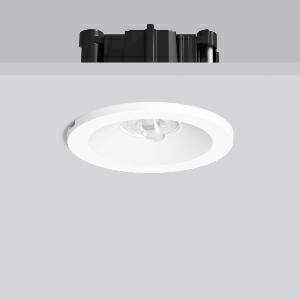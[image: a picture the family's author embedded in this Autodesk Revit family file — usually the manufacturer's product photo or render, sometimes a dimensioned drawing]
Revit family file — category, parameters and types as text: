
# Revit family: turia_l_672562_002_89_3b66
name_source: partatom
category: Lighting Fixtures
units: mm (PartAtom-declared; Revit-internal decimal feet)

## family parameters
Cut with Voids When Loaded = No
Host = Face
Light Source = No
Part Type = Normal
Room Calculation Point = No
Round Connector Dimension = Use Diameter
Shared = No

## types (1)
- TURIA L (1 x LED Modul 765, 250 lm, 6500)
    Apparent Load = 5 VA
    CIE Flux Codes = 70 91 99 100 100
    Color Rendering = 70
    Color Temperature = 6500
    Default Elevation = 1800 mm
    Description = Series: TURIA L
Round emergency luminaire for escape route lighting. With asymmetrical beam plastic lenses for illuminating rescue facilities. Suitable for connection to central battery systems. With MOM monitoring module for LPS (Low Power Supply) small central battery units of the type Easy+IP. With enclosed separate ceiling mounting ring also suitable for ceiling cut-outs of Ø 68 mm. 
Colour: white
Diameter: 62 mm
Height: 3 mm
Cut-out diameter: 54-68 mm
Recess height: 76-162 mm
Luminaire: recess height: 42 mm
Weight: 350 g
Operating mode: non-maintained power mode
Lamp: LED
Socket: without socket
Colour temperature: 6500K
Colour rendering index (CRI): 70
System power: 4.8 W
Rated luminous flux: 250 lm
Luminous flux, emergency: 250 lm
System power, emergency: 4.8 W
Control gear: Regulated power supply
Protection class: II
Type of protection: IP 20
    Height = 0 mm  [stored 0 ft]
    Lamp = 1 x LED Modul 765
    Lamp Light Flux = 250 lm
    Lamp count = 1
    Length = 62 mm  [stored 0.203412 ft]
    Lifetime = 50000 h
    Luminous efficacy = 52 lm/W
    Manufacturer = RZB
    ModVariant = No
    Model = 672562.002.89
    Mounting Place = Ceiling
    Mounting Type = Recessed
    Number of Poles = 1
    OnlyDefault = Yes
    Power Factor = 1
    Product Name = TURIA L
    Product group = Recessed ceiling luminaires
    ProductGroupID = 405
    Protection Class = Protection class II
    Protection Degree = IP 20
    RLX_Detail_Level = 1
    RLX_Emergency_Light_Flux = 250 lm
    RLX_Emergency_Type = 3
    RLX_Emergency_Type_DB = Yes
    RlxData = <blob elided: 54905 chars, md5=a9eec828>
    Socket = socket
    Standby Power = 0 W
    System Light Flux = 250 lm
    System Power = 5 W
    Type Comments = Product without accessories
    Type Image = 672561.002.jpg
    URL = http://relux.com
    VarID = ---
    Voltage = 230 V
    Voltage Range = 220-240 V
    Weight = 0.00 kg
    Width = 0 mm  [stored 0 ft]

note: [stored X ft] marks values corroborated as IEEE doubles in the binary element streams (Revit-internal decimal feet)

## geometry (parser evidence)
native form markers: Blend x4, Sweep x10
no freeform markers — native parametric forms only
